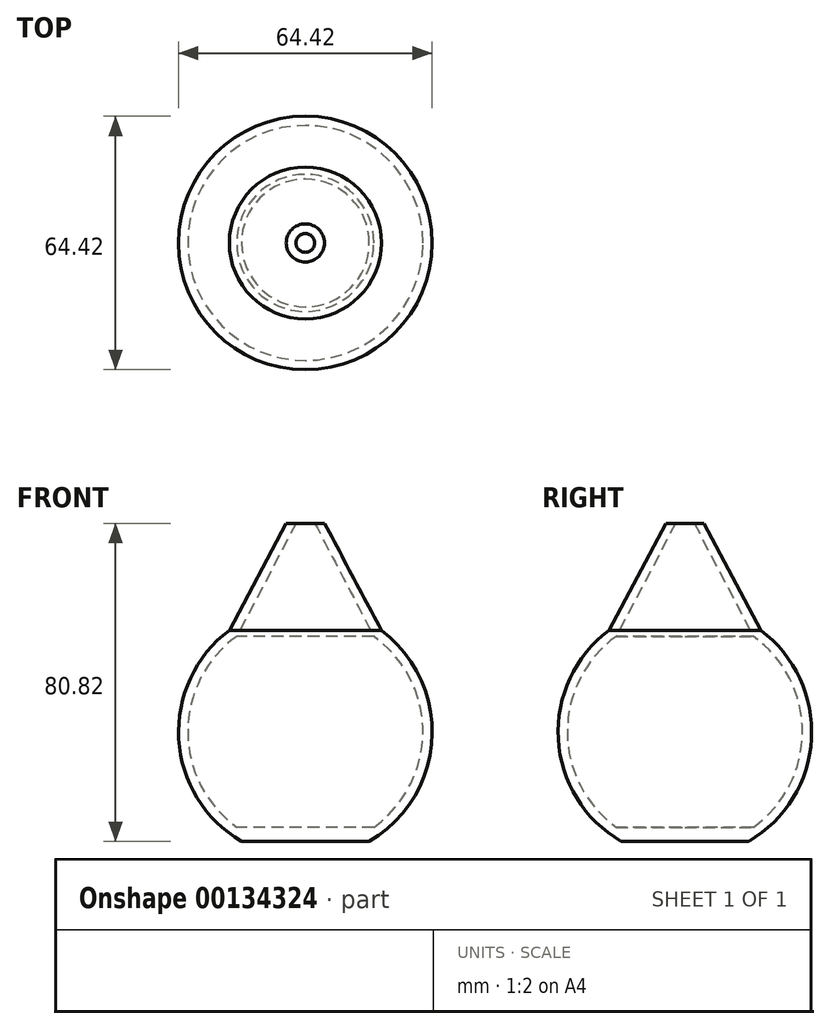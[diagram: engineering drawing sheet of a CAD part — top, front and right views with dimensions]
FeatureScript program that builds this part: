
annotation { "Feature Type Name" : "Feature", "Feature Type Description" : "" }
export const myFeature = defineFeature(function(context is Context, id is Id, definition is map)
    precondition{}
    {
        {
            var Q0;
            Q0=qCreatedBy(makeId("Front.planeOp"),FACE);
            var sketch = newSketch(context, id + "F0", { "sketchPlane" : qUnion([Q0])});
            skArc(sketch, "E0", {"start": v(-19.31, 25.78) * mm, "mid": v(-32.16, -1.85) * mm, "end": v(-16.22, -27.83) * mm});
            skLineSegment(sketch, "E1", {"start": v(-19.31, 25.78) * mm, "end": v(-4.85, 53) * mm});
            skLineSegment(sketch, "E2", {"start": v(-4.85, 53) * mm, "end": v(-2.38, 53) * mm});
            skLineSegment(sketch, "E3", {"start": v(-2.38, 53) * mm, "end": v(-17.41, 24.26) * mm});
            skArc(sketch, "E4", {"start": v(-17.41, 24.26) * mm, "mid": v(-29.86, 0) * mm, "end": v(-17.41, -24.26) * mm});
            skLineSegment(sketch, "E5", {"start": v(-17.41, -24.26) * mm, "end": v(0, -24.26) * mm});
            skLineSegment(sketch, "E6", {"start": v(0, -24.26) * mm, "end": v(0, -27.83) * mm});
            skLineSegment(sketch, "E7", {"start": v(0, -27.83) * mm, "end": v(-16.22, -27.83) * mm});
            skLineSegment(sketch, "E8", {"start": v(0, 64.22) * mm, "end": v(0, -41.96) * mm});
            skSolve(sketch);
        }
        {
            var Q0;
            Q0=makeQuery(id+"F0.imprint","IMPRINT",FACE,{"disambiguationData":[TD([[makeQuery(id+"F0.imprint","IMPRINT",EDGE,{"derivedFrom":sQuery(id+"F0.wireOp",EDGE,"E0")}),1.0]])]});
            var Q1;
            Q1=sQuery(id+"F0.wireOp",EDGE,"E8");
            revolve(context, id + "F1", {"entities" : qUnion([Q0]), "axis" : qUnion([Q1]), "revolveType" : RevolveType.FULL});
        }
    });
